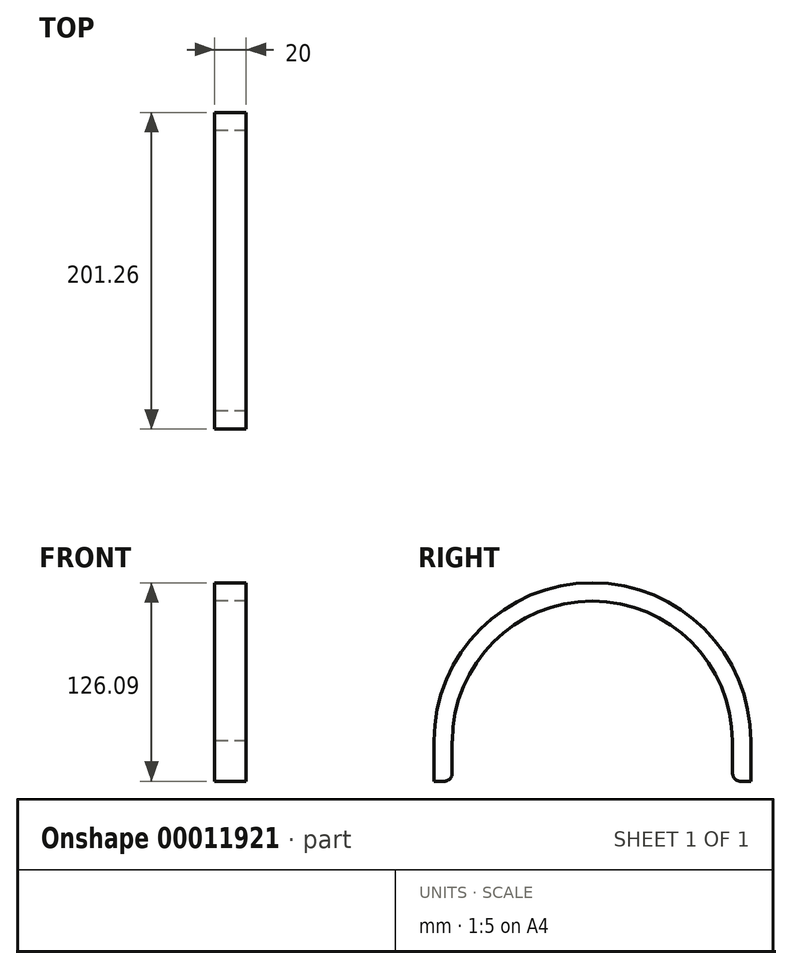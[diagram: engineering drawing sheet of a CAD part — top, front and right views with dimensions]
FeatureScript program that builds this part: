
annotation { "Feature Type Name" : "Feature", "Feature Type Description" : "" }
export const myFeature = defineFeature(function(context is Context, id is Id, definition is map)
    precondition{}
    {
        {
            var Q0;
            Q0=qCreatedBy(makeId("Right.planeOp"),FACE);
            var sketch = newSketch(context, id + "F0", { "sketchPlane" : qUnion([Q0])});
            skCircle(sketch, "E0", {"center": v(0, 0) * mm, "radius": 100.63 * mm});
            skCircle(sketch, "E1", {"center": v(0, 0) * mm, "radius": 88.93 * mm});
            skLineSegment(sketch, "E2.bottom", {"start": v(-100.63, 0) * mm, "end": v(-89.05, 0) * mm});
            skLineSegment(sketch, "E2.top", {"start": v(-100.63, -25.46) * mm, "end": v(-94.05, -25.46) * mm});
            skLineSegment(sketch, "E2.left", {"start": v(-100.63, 0) * mm, "end": v(-100.63, -25.46) * mm});
            skLineSegment(sketch, "E2.right", {"start": v(-89.05, 0) * mm, "end": v(-89.05, -20.46) * mm});
            skLineSegment(sketch, "E3", {"start": v(0, 126.15) * mm, "end": v(0, -128.18) * mm});
            skLineSegment(sketch, "E4.0.MirrorCS", {"start": v(100.63, 0) * mm, "end": v(100.63, -25.46) * mm});
            skLineSegment(sketch, "E5.0.MirrorCS", {"start": v(100.63, -25.46) * mm, "end": v(94.05, -25.46) * mm});
            skLineSegment(sketch, "E6.0.MirrorCS", {"start": v(89.05, 0) * mm, "end": v(89.05, -20.46) * mm});
            skLineSegment(sketch, "E7.0.MirrorCS", {"start": v(100.63, 0) * mm, "end": v(89.05, 0) * mm});
            skPoint(sketch, "E8.visualSharp", {"position": v(-89.05, -25.46) * mm});
            skArc(sketch, "E8.filletArc", {"start": v(-94.05, -25.46) * mm, "mid": v(-90.51, -24) * mm, "end": v(-89.05, -20.46) * mm});
            skPoint(sketch, "E9.visualSharp", {"position": v(89.05, -25.46) * mm});
            skArc(sketch, "E9.filletArc", {"start": v(89.05, -20.46) * mm, "mid": v(90.51, -24) * mm, "end": v(94.05, -25.46) * mm});
            skLineSegment(sketch, "E10", {"start": v(-130.8, 0) * mm, "end": v(132.15, 0) * mm});
            skSolve(sketch);
        }
        {
            var Q0;
            {var subQ0=sQuery(id+"F0.wireOp",EDGE,"E2.left");Q0=makeQuery(id+"F0.imprint","IMPRINT",FACE,{"disambiguationData":[TD([[makeQuery(id+"F0.imprint","IMPRINT",EDGE,{"derivedFrom":subQ0}),1.0]])]});}
            var Q1;
            {var subQ3=sQuery(id+"F0.wireOp",EDGE,"E4.0.MirrorCS");Q1=makeQuery(id+"F0.imprint","IMPRINT",FACE,{"disambiguationData":[TD([[makeQuery(id+"F0.imprint","IMPRINT",EDGE,{"derivedFrom":subQ3}),-1.0]])]});}
            var Q2;
            {var subQ1=sQuery(id+"F0.wireOp",EDGE,"E2.right");Q2=makeQuery(id+"F0.imprint","IMPRINT",FACE,{"disambiguationData":[TD([[makeQuery(id+"F0.imprint","IMPRINT",EDGE,{"derivedFrom":subQ1}),-1.0]])]});}
            var Q3;
            {var subQ1=sQuery(id+"F0.wireOp",EDGE,"E6.0.MirrorCS");Q3=makeQuery(id+"F0.imprint","IMPRINT",FACE,{"disambiguationData":[TD([[makeQuery(id+"F0.imprint","IMPRINT",EDGE,{"derivedFrom":subQ1}),1.0]])]});}
            var Q4;
            {var subQ4=sQuery(id+"F0.wireOp",EDGE,"E1");var subQ6=sQuery(id+"F0.wireOp",EDGE,"E3");var subQ7=makeQuery(id+"F0.imprint","INTERSECT",VERTEX,{"disambiguationData":[OD(0.0)],"derivedFrom":[subQ4,subQ6]});Q4=makeQuery(id+"F0.imprint","IMPRINT",FACE,{"disambiguationData":[TD([[makeQuery(id+"F0.imprint","IMPRINT",EDGE,{"disambiguationData":[TD([[subQ7,1.0]])],"derivedFrom":subQ4}),-1.0]])]});}
            var Q5;
            {var subQ1=sQuery(id+"F0.wireOp",EDGE,"E1");var subQ6=sQuery(id+"F0.wireOp",EDGE,"E3");var subQ7=makeQuery(id+"F0.imprint","INTERSECT",VERTEX,{"disambiguationData":[OD(0.0)],"derivedFrom":[subQ1,subQ6]});Q5=makeQuery(id+"F0.imprint","IMPRINT",FACE,{"disambiguationData":[TD([[makeQuery(id+"F0.imprint","IMPRINT",EDGE,{"disambiguationData":[TD([[subQ7,-1.0]])],"derivedFrom":subQ1}),-1.0]])]});}
            extrude(context, id + "F1", {"entities" : qUnion([Q0, Q1, Q2, Q3, Q4, Q5]), "depth" : 20 * mm, "symmetric" : true});
        }
    });
